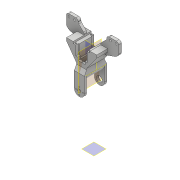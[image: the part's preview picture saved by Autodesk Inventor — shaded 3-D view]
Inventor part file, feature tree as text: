
AUTODESK INVENTOR PART (.ipt)
format: ipt  version: 2018 (Build 220112000, 112)  size: 451,072 bytes
history: native  units: mm
features: extrude x19, sketch x17, mirror x5, plane x4, fillet x3, chamfer x2
ambient origin geometry x8: Origin, YZ Plane, XZ Plane, XY Plane, X Axis, Y Axis, Z Axis, Center Point
bodies: Solid1 (feature_tree)
feature tree (50):
  extrude  "base"  Depth=32.0mm
  extrude  "servo_place"  Depth=11.5mm
  extrude  "screws_servo"  Depth=6.25mm
  plane  "Work Plane1"
  extrude  "pilars_top"  Depth=12.5mm
  extrude  "base_top"  Depth=18.0mm
  extrude  "screw_hole"  Depth=2.8mm
  plane  "Work Plane2"
  extrude  "connector_prev_servo"  Depth=17.0mm TaperAngle=0.0deg
  chamfer  "Chamfer2"  Distance=20.0mm
  fillet  "Fillet3"  Radius=18.0mm
  extrude  "screw_holes"  Depth=5.0mm TaperAngle=0.0deg
  fillet  "Fillet4"  Radius=5.0mm
  extrude  "Extrusion14"  Depth=5.0mm
  extrude  "Extrusion16"  Depth=5.0mm
  plane  "Work Plane3"
  plane  "Work Plane4"
  mirror  "Mirror1"
  mirror  "Mirror2"
  extrude  "Extrusion18"  Depth=4.0mm
  extrude  "Extrusion19"  Depth=36.0mm TaperAngle=0.0deg
  extrude  "Extrusion20"  Depth=4.0mm
  mirror  "Mirror3"
  mirror  "Mirror4"
  extrude  "Extrusion21"  Depth=6.0mm
  extrude  "Extrusion22"  Depth=20.0mm TaperAngle=360.0deg
  chamfer  "Chamfer3"  Distance=20.0mm
  extrude  "Extrusion23"  Depth=10.5mm
  extrude  "Extrusion11"  Depth=25.0mm
  extrude  "Extrusion24"  Depth=5.0mm TaperAngle=0.0deg
  fillet  "Fillet5"  [1 undecoded]
  mirror  "Mirror5"
  extrude  "Extrusion25"  [1 undecoded]
  sketch  "Sketch1"  dims[d0=18.0mm d1=32.0mm]
  sketch  "Sketch2"  dims[d2=25.0mm d3=0.0mm d4=11.5mm]
  sketch  "Sketch3"  dims[d5=90.0deg d6=6.25mm]
  sketch  "Sketch6"  dims[d7=23.0mm d8=12.5mm]
  sketch  "Sketch9"  dims[d9=18.0mm d10=0.0mm d11=2.8mm]
  sketch  "Sketch12"  dims[d12=2.0mm d13=2.8mm]
  sketch  "Sketch13"  dims[d14=2.0mm d15=17.0mm d16=0.0mm d26=20.0mm d27=0.0mm d39=18.0mm]
  sketch  "Sketch14"  dims[d40=18.0mm d41=5.0mm d42=0.0mm d47=5.0mm d48=0.0mm]
  sketch  "Sketch16"  dims[d55=5.0mm d56=0.0mm d60=2.5mm]
  sketch  "Sketch18"  dims[d61=5.0mm d62=5.0mm]
  sketch  "Sketch19"  dims[d63=-10.0mm d64=4.0mm]
  sketch  "Sketch20"  dims[d65=4.0mm d66=36.0mm d67=0.0mm]
  sketch  "Sketch21"  dims[d68=8.0mm d69=4.0mm d70=45.0deg d71=9.0mm]
  sketch  "Sketch22"  dims[d72=5.5mm d73=6.0mm]
  sketch  "Sketch23"  dims[d74=2.0mm d75=40.0mm d77=360.0deg d79=20.0mm d80=0.0mm]
  sketch  "Sketch24"  dims[d81=9.0mm d82=10.5mm]
  sketch  "Sketch25"  dims[d83=20.0mm d84=0.0mm d95=25.0mm d96=4.6mm d97=0.0mm d98=-16.0mm d99=-9.0mm d100=12.5mm d105=5.0mm d106=10.0mm d107=20.0mm d108=10.0mm d109=0.0mm d110=5.0mm d111=30.0mm d112=3.0mm d113=0.0mm d114=2.5mm d115=2.5mm d116=2.8mm d117=5.0mm d118=0.0mm d119=11.75mm d120=12.5mm d121=23.5mm d122=12.5mm d123=10.0mm d124=0.0mm d125=7.0mm d126=10.0mm d127=0.0mm d128=8.0mm d129=4.0mm d130=45.0deg d131=27.0mm d132=27.0mm d133=10.0mm d134=0.0mm d135=10.0mm d136=15.0mm d137=3.5mm d138=10.0mm d139=3.5mm d140=3.0mm d141=15.0mm d142=135.0deg d143=6.0mm d144=21.0mm d145=20.0mm d146=6.0mm d147=5.0mm d148=0.0mm d149=4.0mm d150=12.5mm d151=25.0mm d152=5.0mm d153=0.0mm]
note: 2 required parameter values undecoded (feature->parameter linkage not recoverable at this tier; creation-order binding heuristic only, values carry confidence <= 0.55)
